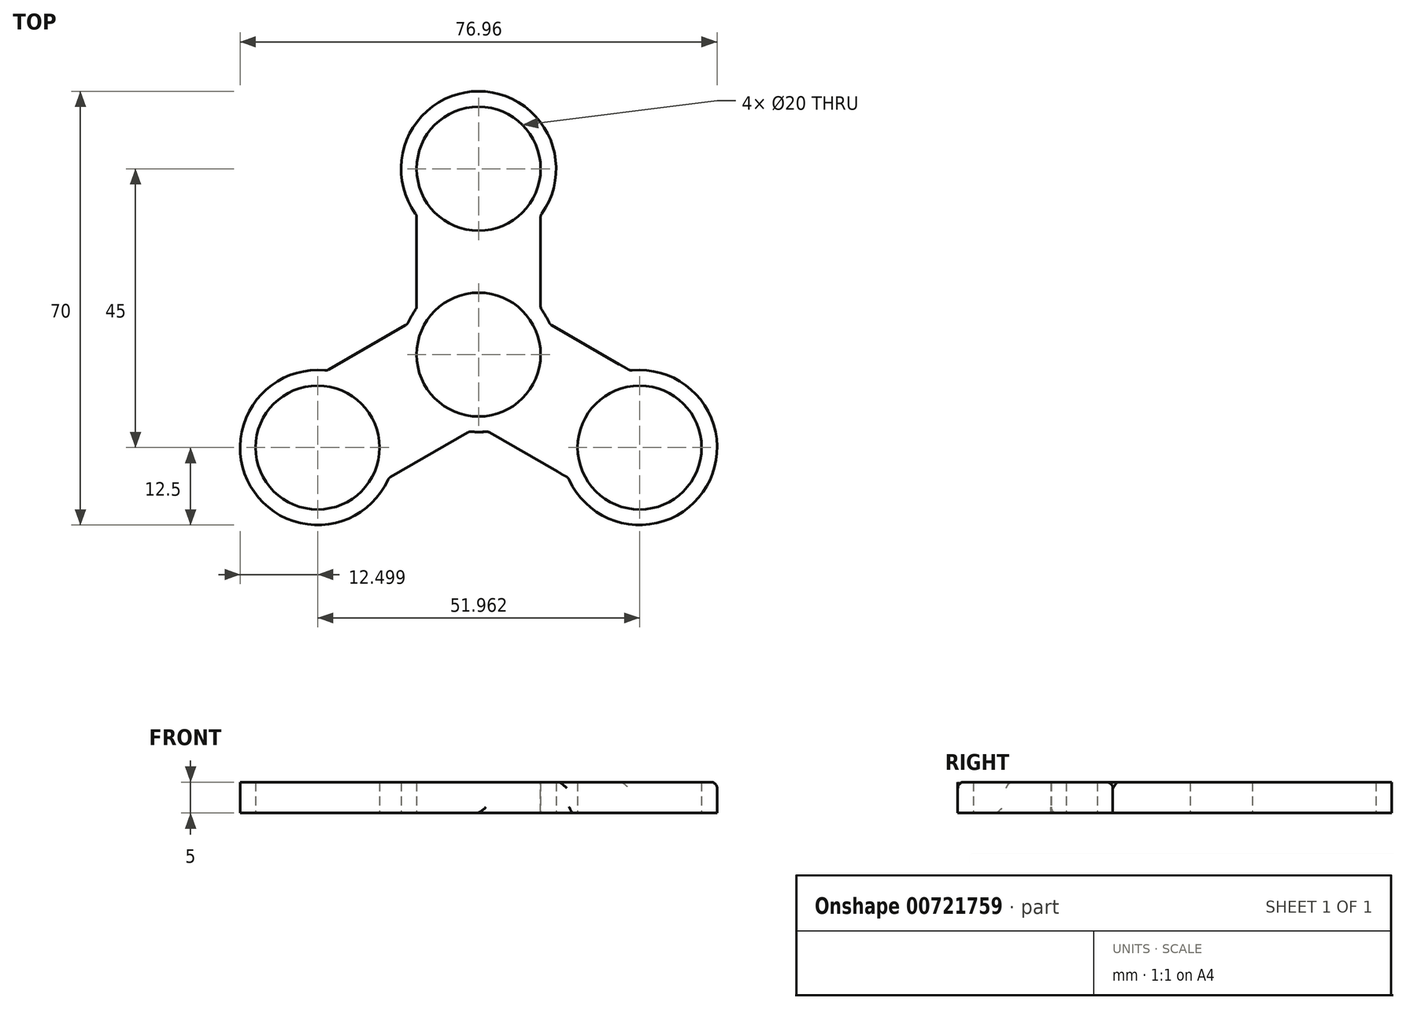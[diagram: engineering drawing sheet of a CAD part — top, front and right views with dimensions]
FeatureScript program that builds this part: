
annotation { "Feature Type Name" : "Feature", "Feature Type Description" : "" }
export const myFeature = defineFeature(function(context is Context, id is Id, definition is map)
    precondition{}
    {
        {
            var Q0;
            Q0=qCreatedBy(makeId("Top.planeOp"),FACE);
            var sketch = newSketch(context, id + "F0", { "sketchPlane" : qUnion([Q0])});
            skCircle(sketch, "E0", {"center": v(0, 0) * mm, "radius": 10 * mm});
            skCircle(sketch, "E1", {"center": v(0, 0) * mm, "radius": 12.5 * mm});
            skLineSegment(sketch, "E2.bottom", {"start": v(-10, 0) * mm, "end": v(10, 0) * mm});
            skLineSegment(sketch, "E2.top", {"start": v(-10, 30) * mm, "end": v(10, 30) * mm});
            skLineSegment(sketch, "E2.left", {"start": v(-10, 0) * mm, "end": v(-10, 30) * mm});
            skLineSegment(sketch, "E2.right", {"start": v(10, 0) * mm, "end": v(10, 30) * mm});
            skCircle(sketch, "E3", {"center": v(0, 30) * mm, "radius": 10 * mm});
            skCircle(sketch, "E4", {"center": v(0, 30) * mm, "radius": 12.5 * mm});
            skSolve(sketch);
        }
        {
            var Q0;
            Q0 = qSketchRegion(id + "F0", true);
            extrude(context, id + "F1", {"entities" : qUnion([Q0]), "depth" : 5 * mm, "offsetDistance" : 25 * mm});
        }
        {
            var Q0;
            Q0=makeQuery(id+"F1.opExtrude","SWEPT_BODY",BODY,{"disambiguationData":[OSD([sQuery(id+"F0.wireOp",EDGE,"E0"),sQuery(id+"F0.wireOp",EDGE,"E1"),sQuery(id+"F0.wireOp",EDGE,"E2.left"),sQuery(id+"F0.wireOp",EDGE,"E2.right"),sQuery(id+"F0.wireOp",EDGE,"E3"),sQuery(id+"F0.wireOp",EDGE,"E4")])]});
            var Q1;
            Q1=makeQuery(id+"F1.opExtrude","CAP_EDGE",EDGE,{"disambiguationData":[OSD([sQuery(id+"F0.wireOp",EDGE,"E0")])],"isStart":true});
            circularPattern(context, id + "F2", {"entities" : qUnion([Q0]), "axis" : qUnion([Q1]), "angle" : 360 * degree, "instanceCount" : 3, "equalSpace" : true});
        }
        {
            var Q0;
            Q0=makeQuery(id+"F2.opPattern","COPY",BODY,{"derivedFrom":makeQuery(id+"F1.opExtrude","SWEPT_BODY",BODY,{"disambiguationData":[OSD([sQuery(id+"F0.wireOp",EDGE,"E0"),sQuery(id+"F0.wireOp",EDGE,"E1"),sQuery(id+"F0.wireOp",EDGE,"E2.left"),sQuery(id+"F0.wireOp",EDGE,"E2.right"),sQuery(id+"F0.wireOp",EDGE,"E3"),sQuery(id+"F0.wireOp",EDGE,"E4")])]}),"instanceName":"1"});
            var Q1;
            Q1=makeQuery(id+"F1.opExtrude","SWEPT_BODY",BODY,{"disambiguationData":[OSD([sQuery(id+"F0.wireOp",EDGE,"E0"),sQuery(id+"F0.wireOp",EDGE,"E1"),sQuery(id+"F0.wireOp",EDGE,"E2.left"),sQuery(id+"F0.wireOp",EDGE,"E2.right"),sQuery(id+"F0.wireOp",EDGE,"E3"),sQuery(id+"F0.wireOp",EDGE,"E4")])]});
            var Q2;
            Q2=makeQuery(id+"F2.opPattern","COPY",BODY,{"derivedFrom":makeQuery(id+"F1.opExtrude","SWEPT_BODY",BODY,{"disambiguationData":[OSD([sQuery(id+"F0.wireOp",EDGE,"E0"),sQuery(id+"F0.wireOp",EDGE,"E1"),sQuery(id+"F0.wireOp",EDGE,"E2.left"),sQuery(id+"F0.wireOp",EDGE,"E2.right"),sQuery(id+"F0.wireOp",EDGE,"E3"),sQuery(id+"F0.wireOp",EDGE,"E4")])]}),"instanceName":"2"});
            booleanBodies(context, id + "F3", {"operationType" : BooleanOperationType.UNION, "tools" : qUnion([Q0, Q1, Q2])});
        }
        {
            var Q0;
            Q0=makeQuery(id+"F2.opPattern","COPY",EDGE,{"derivedFrom":makeQuery(id+"F1.opExtrude","SWEPT_EDGE",EDGE,{"disambiguationData":[OSD([sQuery(id+"F0.wireOp",EDGE,"E2.left"),sQuery(id+"F0.wireOp",EDGE,"E4")])]}),"instanceName":"1"});
            var Q1;
            Q1=makeQuery(id+"F2.opPattern","COPY",EDGE,{"derivedFrom":makeQuery(id+"F1.opExtrude","SWEPT_EDGE",EDGE,{"disambiguationData":[OSD([sQuery(id+"F0.wireOp",EDGE,"E1"),sQuery(id+"F0.wireOp",EDGE,"E2.left")])]}),"instanceName":"1"});
            var Q2;
            {var subQ0=makeQuery(id+"F1.opExtrude","SWEPT_FACE",FACE,{"disambiguationData":[OSD([sQuery(id+"F0.wireOp",EDGE,"E1")])]});var subQ1=makeQuery(id+"F2.opPattern","COPY",FACE,{"derivedFrom":subQ0,"instanceName":"1"});Q2=makeQuery(id+"F3.opBoolean","INTERSECT",EDGE,{"disambiguationData":[topologyDisambiguationEdgeConnected([makeQuery(id+"F2.opPattern","COPY",FACE,{"derivedFrom":makeQuery(id+"F1.opExtrude","SWEPT_FACE",FACE,{"disambiguationData":[OSD([sQuery(id+"F0.wireOp",EDGE,"E2.right")])]}),"instanceName":"2"})])],"derivedFrom":[subQ0,subQ1]});}
            var Q3;
            Q3=makeQuery(id+"F2.opPattern","COPY",EDGE,{"derivedFrom":makeQuery(id+"F1.opExtrude","SWEPT_EDGE",EDGE,{"disambiguationData":[OSD([sQuery(id+"F0.wireOp",EDGE,"E2.right"),sQuery(id+"F0.wireOp",EDGE,"E4")])]}),"instanceName":"2"});
            var Q4;
            Q4=makeQuery(id+"F2.opPattern","COPY",EDGE,{"derivedFrom":makeQuery(id+"F1.opExtrude","SWEPT_EDGE",EDGE,{"disambiguationData":[OSD([sQuery(id+"F0.wireOp",EDGE,"E2.left"),sQuery(id+"F0.wireOp",EDGE,"E4")])]}),"instanceName":"2"});
            var Q5;
            {var subQ0=makeQuery(id+"F1.opExtrude","SWEPT_FACE",FACE,{"disambiguationData":[OSD([sQuery(id+"F0.wireOp",EDGE,"E1")])]});var subQ1=makeQuery(id+"F2.opPattern","COPY",FACE,{"derivedFrom":subQ0,"instanceName":"1"});Q5=makeQuery(id+"F3.opBoolean","INTERSECT",EDGE,{"disambiguationData":[topologyDisambiguationEdgeConnected([makeQuery(id+"F2.opPattern","COPY",FACE,{"derivedFrom":makeQuery(id+"F1.opExtrude","SWEPT_FACE",FACE,{"disambiguationData":[OSD([sQuery(id+"F0.wireOp",EDGE,"E2.left")])]}),"instanceName":"2"})])],"derivedFrom":[subQ0,subQ1]});}
            var Q6;
            {var subQ0=makeQuery(id+"F1.opExtrude","SWEPT_FACE",FACE,{"disambiguationData":[OSD([sQuery(id+"F0.wireOp",EDGE,"E1")])]});var subQ1=makeQuery(id+"F2.opPattern","COPY",FACE,{"derivedFrom":subQ0,"instanceName":"1"});Q6=makeQuery(id+"F3.opBoolean","INTERSECT",EDGE,{"disambiguationData":[topologyDisambiguationEdgeConnected([makeQuery(id+"F1.opExtrude","SWEPT_FACE",FACE,{"disambiguationData":[OSD([sQuery(id+"F0.wireOp",EDGE,"E2.right")])]})])],"derivedFrom":[subQ1,makeQuery(id+"F2.opPattern","COPY",FACE,{"derivedFrom":subQ0,"instanceName":"2"})]});}
            var Q7;
            Q7=makeQuery(id+"F1.opExtrude","SWEPT_EDGE",EDGE,{"disambiguationData":[OSD([sQuery(id+"F0.wireOp",EDGE,"E2.right"),sQuery(id+"F0.wireOp",EDGE,"E4")])]});
            var Q8;
            Q8=makeQuery(id+"F1.opExtrude","SWEPT_EDGE",EDGE,{"disambiguationData":[OSD([sQuery(id+"F0.wireOp",EDGE,"E2.left"),sQuery(id+"F0.wireOp",EDGE,"E4")])]});
            var Q9;
            {var subQ0=makeQuery(id+"F1.opExtrude","SWEPT_FACE",FACE,{"disambiguationData":[OSD([sQuery(id+"F0.wireOp",EDGE,"E1")])]});var subQ1=makeQuery(id+"F2.opPattern","COPY",FACE,{"derivedFrom":subQ0,"instanceName":"1"});Q9=makeQuery(id+"F3.opBoolean","INTERSECT",EDGE,{"disambiguationData":[topologyDisambiguationEdgeConnected([makeQuery(id+"F1.opExtrude","SWEPT_FACE",FACE,{"disambiguationData":[OSD([sQuery(id+"F0.wireOp",EDGE,"E2.left")])]})])],"derivedFrom":[subQ1,makeQuery(id+"F2.opPattern","COPY",FACE,{"derivedFrom":subQ0,"instanceName":"2"})]});}
            var Q10;
            Q10=makeQuery(id+"F2.opPattern","COPY",EDGE,{"derivedFrom":makeQuery(id+"F1.opExtrude","SWEPT_EDGE",EDGE,{"disambiguationData":[OSD([sQuery(id+"F0.wireOp",EDGE,"E1"),sQuery(id+"F0.wireOp",EDGE,"E2.right")])]}),"instanceName":"1"});
            var Q11;
            Q11=makeQuery(id+"F2.opPattern","COPY",EDGE,{"derivedFrom":makeQuery(id+"F1.opExtrude","SWEPT_EDGE",EDGE,{"disambiguationData":[OSD([sQuery(id+"F0.wireOp",EDGE,"E2.right"),sQuery(id+"F0.wireOp",EDGE,"E4")])]}),"instanceName":"1"});
            var Q12;
            Q12=makeQuery(id+"F2.opPattern","COPY",EDGE,{"derivedFrom":makeQuery(id+"F1.opExtrude","CAP_EDGE",EDGE,{"disambiguationData":[OSD([sQuery(id+"F0.wireOp",EDGE,"E4")])],"isStart":false}),"instanceName":"2"});
            var Q13;
            Q13=makeQuery(id+"F2.opPattern","COPY",EDGE,{"derivedFrom":makeQuery(id+"F1.opExtrude","CAP_EDGE",EDGE,{"disambiguationData":[OSD([sQuery(id+"F0.wireOp",EDGE,"E2.right")])],"isStart":true}),"instanceName":"2"});
            fillet(context, id + "F4", {"entities" : qUnion([Q0, Q1, Q2, Q3, Q4, Q5, Q6, Q7, Q8, Q9, Q10, Q11, Q12, Q13]), "radius" : 1 * mm, "tangentPropagation" : true, "allowEdgeOverflow" : false});
        }
    });
